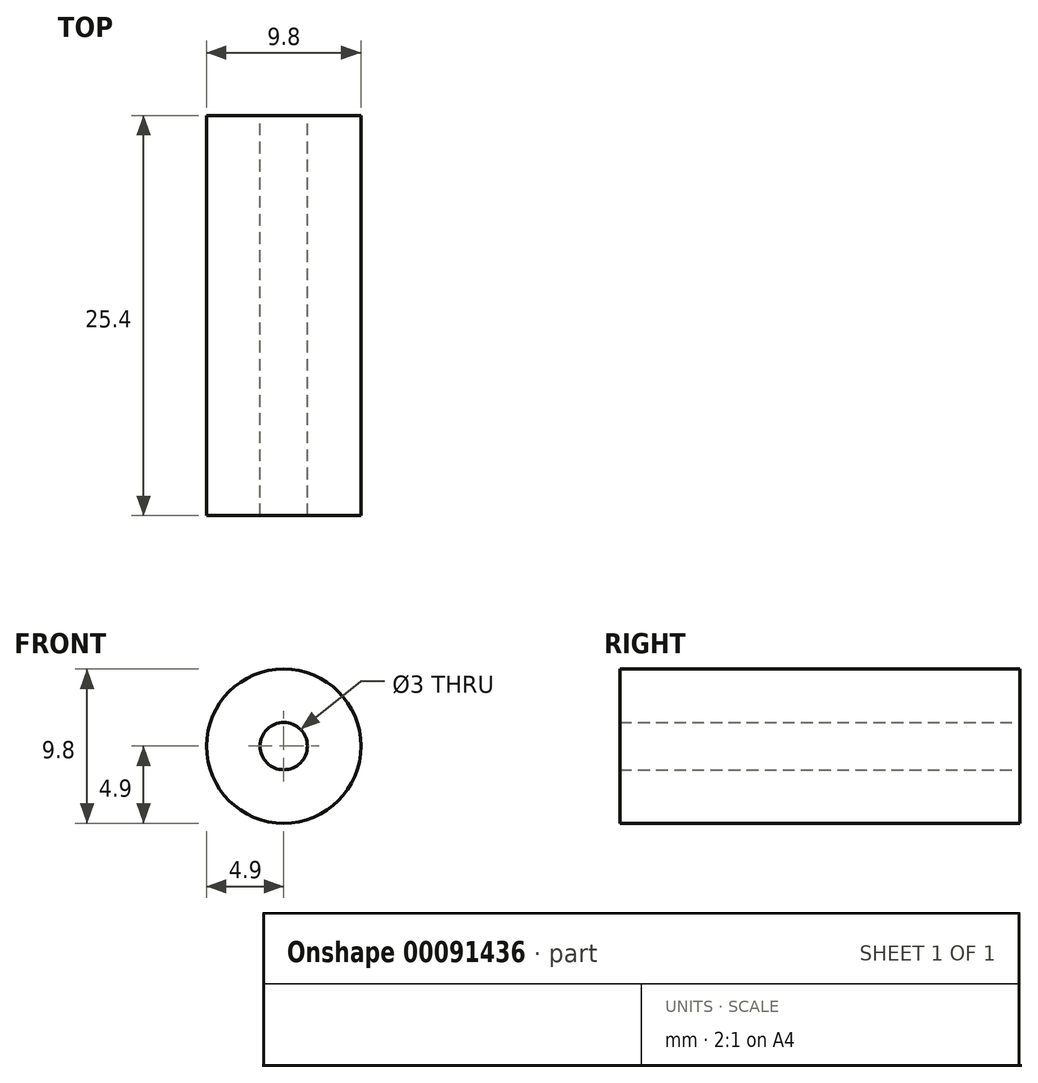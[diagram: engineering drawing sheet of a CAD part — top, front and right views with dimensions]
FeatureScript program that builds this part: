
annotation { "Feature Type Name" : "Feature", "Feature Type Description" : "" }
export const myFeature = defineFeature(function(context is Context, id is Id, definition is map)
    precondition{}
    {
        {
            var Q0;
            Q0=qCreatedBy(makeId("Front.planeOp"),FACE);
            var sketch = newSketch(context, id + "F0", { "sketchPlane" : qUnion([Q0])});
            skCircle(sketch, "E0", {"center": v(0, 0) * mm, "radius": 4.9 * mm});
            skSolve(sketch);
        }
        {
            var Q0;
            Q0=makeQuery(id+"F0.imprint","IMPRINT",FACE,{"disambiguationData":[TD([[makeQuery(id+"F0.imprint","IMPRINT",EDGE,{"derivedFrom":sQuery(id+"F0.wireOp",EDGE,"E0")}),1.0]])]});
            extrude(context, id + "F1", {"entities" : qUnion([Q0]), "depth" : 25.4 * mm});
        }
        {
            var Q0;
            Q0=sQuery(id+"F0.wireOp",VERTEX,"E0.center");
            var Q1;
            Q1=makeQuery(id+"F1.opExtrude","SWEPT_BODY",BODY,{"disambiguationData":[OSD([sQuery(id+"F0.wireOp",EDGE,"E0")])]});
            hole(context, id + "F2", {"style" : HoleStyle.SIMPLE, "endStyle" : HoleEndStyle.THROUGH, "oppositeDirection" : true, "holeDiameter" : 3 * mm, "locations" : qUnion([Q0]), "scope" : qUnion([Q1]), "isTappedThrough" : true});
        }
    });
